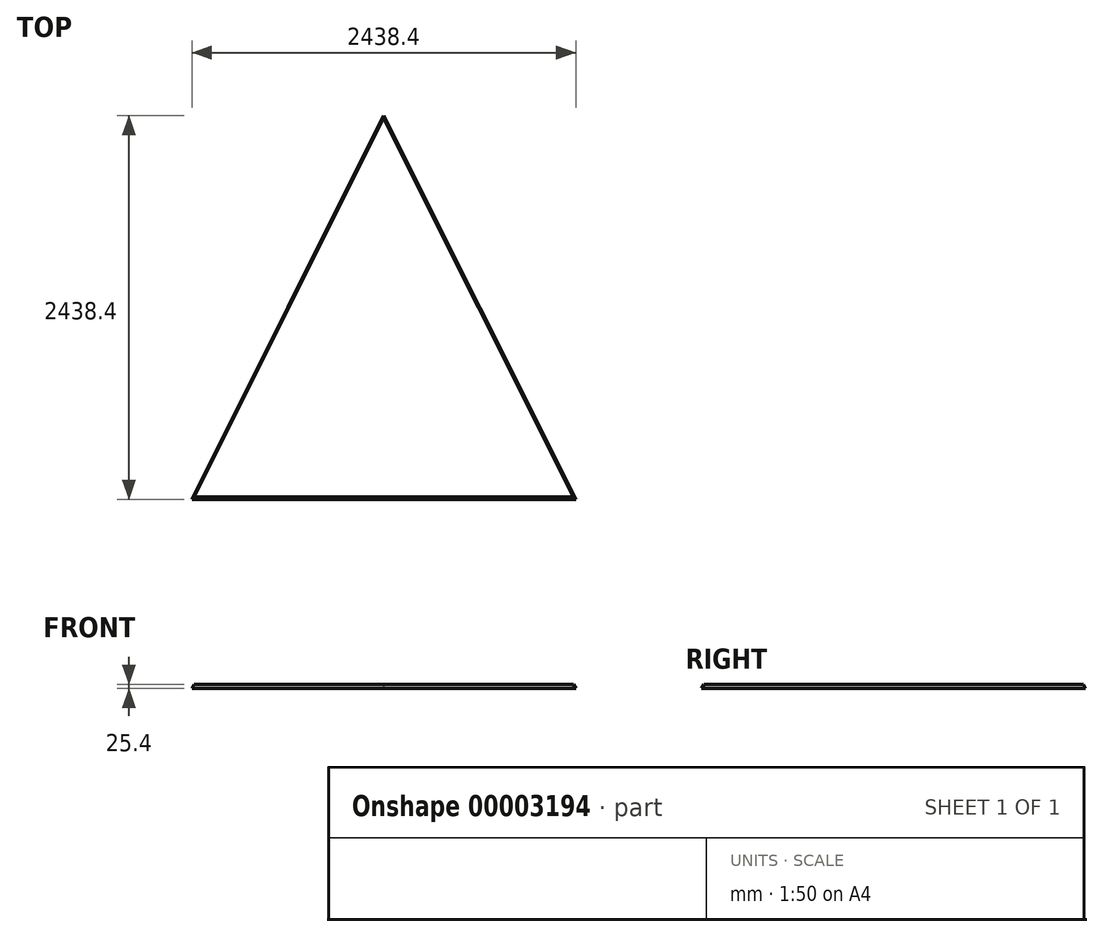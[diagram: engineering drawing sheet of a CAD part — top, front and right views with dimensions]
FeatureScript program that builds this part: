
annotation { "Feature Type Name" : "Feature", "Feature Type Description" : "" }
export const myFeature = defineFeature(function(context is Context, id is Id, definition is map)
    precondition{}
    {
        {
            var Q0;
            Q0=qCreatedBy(makeId("Top.planeOp"),FACE);
            var sketch = newSketch(context, id + "F0", { "sketchPlane" : qUnion([Q0])});
            skLineSegment(sketch, "E0", {"start": v(-1211.78, -585.02) * mm, "end": v(1226.62, -585.02) * mm});
            skLineSegment(sketch, "E1", {"start": v(-1211.78, -585.02) * mm, "end": v(7.42, 1853.38) * mm});
            skLineSegment(sketch, "E2", {"start": v(1226.62, -585.02) * mm, "end": v(7.42, 1853.38) * mm});
            skPoint(sketch, "E3", {"position": v(7.42, -585.02) * mm});
            skSolve(sketch);
        }
        {
            var Q0;
            Q0=makeQuery(id+"F0.imprint","IMPRINT",FACE,{"disambiguationData":[TD([[makeQuery(id+"F0.imprint","IMPRINT",EDGE,{"derivedFrom":sQuery(id+"F0.wireOp",EDGE,"E0")}),1.0]])]});
            extrude(context, id + "F1", {"entities" : qUnion([Q0]), "depth" : 25.4 * mm});
        }
        {
            var Q0;
            Q0=makeQuery(id+"F1.opExtrude","CAP_EDGE",EDGE,{"disambiguationData":[OSD([sQuery(id+"F0.wireOp",EDGE,"E0")])],"isStart":false});
            chamfer(context, id + "F2", {"entities" : qUnion([Q0]), "chamferType" : ChamferType.OFFSET_ANGLE, "width" : 25.4 * mm, "oppositeDirection" : true, "angle" : 30 * degree, "tangentPropagation" : true});
        }
        {
            var Q0;
            Q0=makeQuery(id+"F1.opExtrude","CAP_EDGE",EDGE,{"disambiguationData":[OSD([sQuery(id+"F0.wireOp",EDGE,"E2")])],"isStart":false});
            chamfer(context, id + "F3", {"entities" : qUnion([Q0]), "chamferType" : ChamferType.OFFSET_ANGLE, "width" : 25.4 * mm, "oppositeDirection" : true, "angle" : 15 * degree, "tangentPropagation" : true});
        }
        {
            var Q0;
            Q0=makeQuery(id+"F1.opExtrude","CAP_EDGE",EDGE,{"disambiguationData":[OSD([sQuery(id+"F0.wireOp",EDGE,"E1")])],"isStart":false});
            chamfer(context, id + "F4", {"entities" : qUnion([Q0]), "chamferType" : ChamferType.OFFSET_ANGLE, "width" : 25.4 * mm, "oppositeDirection" : false, "angle" : 15 * degree, "tangentPropagation" : true});
        }
    });
